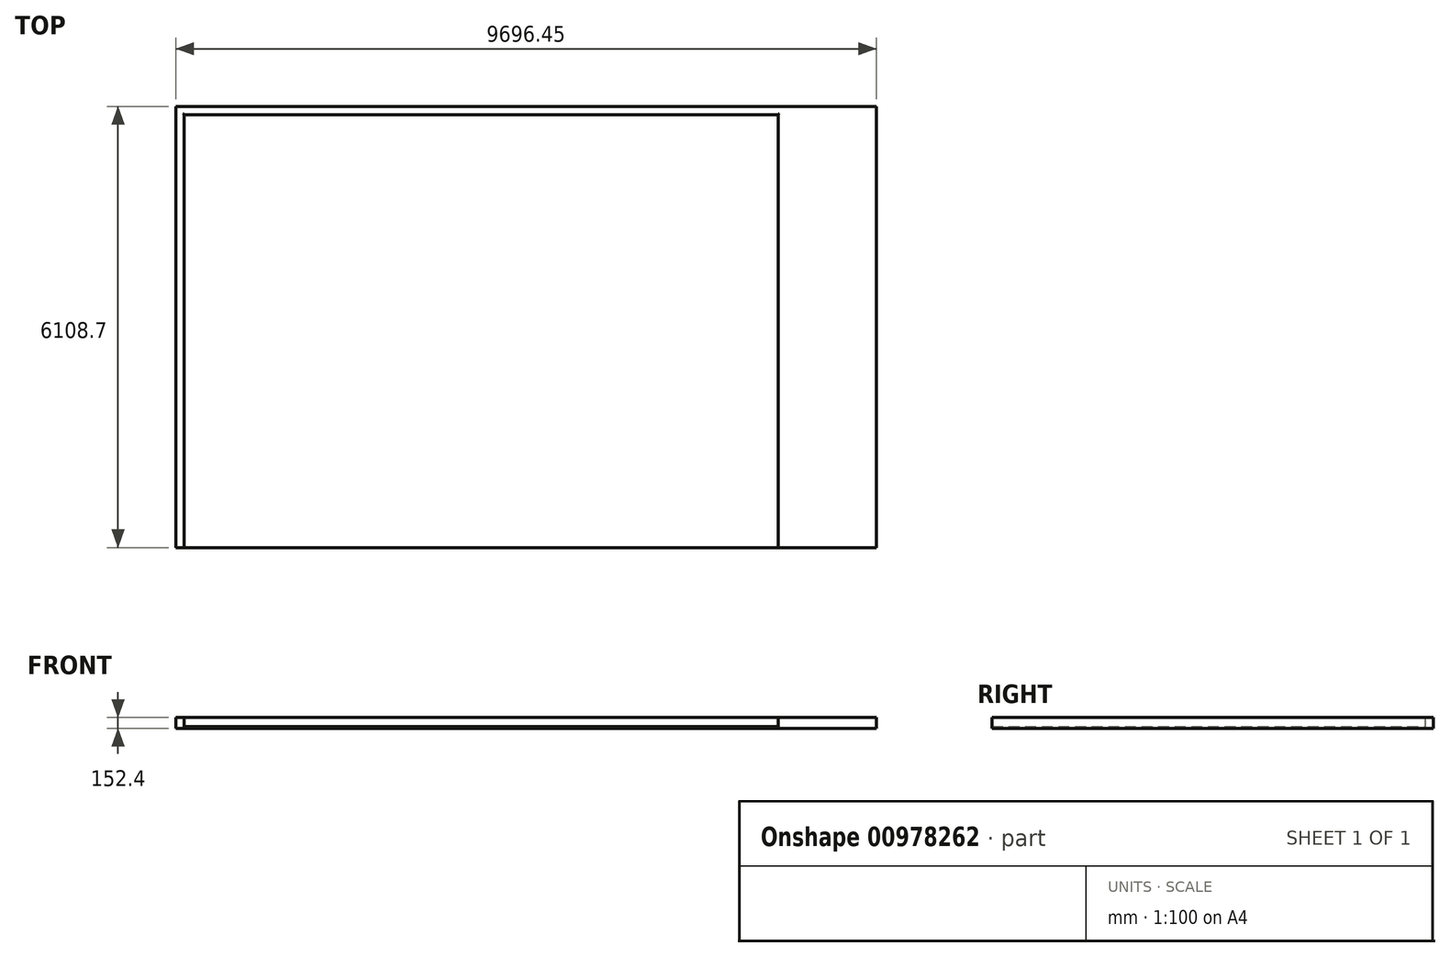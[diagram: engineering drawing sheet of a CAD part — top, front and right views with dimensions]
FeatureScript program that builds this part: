
annotation { "Feature Type Name" : "Feature", "Feature Type Description" : "" }
export const myFeature = defineFeature(function(context is Context, id is Id, definition is map)
    precondition{}
    {
        {
            var Q0;
            Q0=qCreatedBy(makeId("Top.planeOp"),FACE);
            var sketch = newSketch(context, id + "F0", { "sketchPlane" : qUnion([Q0])});
            skLineSegment(sketch, "E0.bottom", {"start": v(0, 0) * mm, "end": v(-9493.25, 0) * mm});
            skLineSegment(sketch, "E0.top", {"start": v(-1270, 5994.4) * mm, "end": v(-9493.25, 5994.4) * mm});
            skLineSegment(sketch, "E0.left", {"start": v(-1270, 0) * mm, "end": v(-1270, 5994.4) * mm});
            skLineSegment(sketch, "E0.right", {"start": v(-9493.25, 0) * mm, "end": v(-9493.25, 5994.4) * mm});
            skLineSegment(sketch, "E1.bottom", {"start": v(88.9, 0) * mm, "end": v(-9607.55, 0) * mm});
            skLineSegment(sketch, "E1.top", {"start": v(88.9, 6108.7) * mm, "end": v(-9607.55, 6108.7) * mm});
            skLineSegment(sketch, "E1.left", {"start": v(88.9, 0) * mm, "end": v(88.9, 6108.7) * mm});
            skLineSegment(sketch, "E1.right", {"start": v(-9607.55, 0) * mm, "end": v(-9607.55, 6108.7) * mm});
            skSolve(sketch);
        }
        {
            var Q0;
            Q0=makeQuery(id+"F0.imprint","IMPRINT",FACE,{"disambiguationData":[TD([[makeQuery(id+"F0.imprint","IMPRINT",EDGE,{"derivedFrom":sQuery(id+"F0.wireOp",EDGE,"E0.top")}),1.0]])]});
            extrude(context, id + "F1", {"entities" : qUnion([Q0]), "depth" : 25.4 * mm, "offsetDistance" : 25.4 * mm});
        }
        {
            var Q0;
            Q0=makeQuery(id+"F0.imprint","IMPRINT",FACE,{"disambiguationData":[TD([[makeQuery(id+"F0.imprint","IMPRINT",EDGE,{"derivedFrom":sQuery(id+"F0.wireOp",EDGE,"E0.top")}),-1.0]])]});
            extrude(context, id + "F2", {"entities" : qUnion([Q0]), "operationType" : NewBodyOperationType.ADD, "depth" : 152.4 * mm, "offsetDistance" : 25.4 * mm});
        }
        {
            var Q0;
            Q0=makeQuery(id+"F2.opExtrude","CAP_EDGE",EDGE,{"disambiguationData":[OSD([sQuery(id+"F0.wireOp",EDGE,"E0.left")])],"isStart":false});
            var Q1;
            Q1=makeQuery(id+"F1.opExtrude","CAP_EDGE",EDGE,{"disambiguationData":[OSD([sQuery(id+"F0.wireOp",EDGE,"E0.left")])],"isStart":false});
            var Q2;
            Q2=makeQuery(id+"F1.opExtrude","CAP_EDGE",EDGE,{"disambiguationData":[OSD([sQuery(id+"F0.wireOp",EDGE,"E0.top")])],"isStart":false});
            var Q3;
            Q3=makeQuery(id+"F1.opExtrude","CAP_EDGE",EDGE,{"disambiguationData":[OSD([sQuery(id+"F0.wireOp",EDGE,"E0.right")])],"isStart":false});
            var Q4;
            Q4=makeQuery(id+"F2.opExtrude","CAP_EDGE",EDGE,{"disambiguationData":[OSD([sQuery(id+"F0.wireOp",EDGE,"E0.right")])],"isStart":false});
            var Q5;
            Q5=makeQuery(id+"F2.opExtrude","CAP_EDGE",EDGE,{"disambiguationData":[OSD([sQuery(id+"F0.wireOp",EDGE,"E0.top")])],"isStart":false});
            fillet(context, id + "F3", {"entities" : qUnion([Q0, Q1, Q2, Q3, Q4, Q5]), "radius" : 12.7 * mm, "tangentPropagation" : true, "allowEdgeOverflow" : false});
        }
    });
